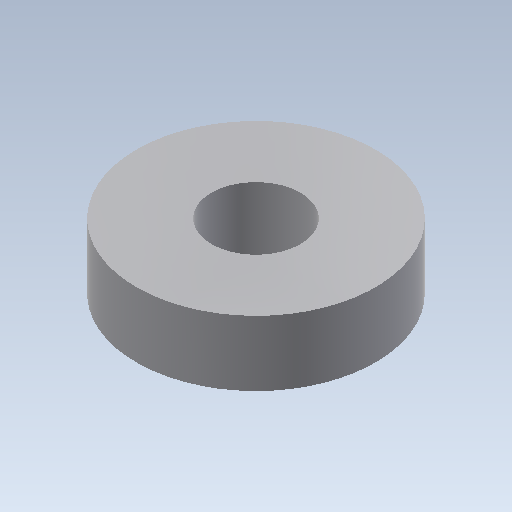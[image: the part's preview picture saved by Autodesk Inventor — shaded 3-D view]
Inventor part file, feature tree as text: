
AUTODESK INVENTOR PART (.ipt)
format: ipt  version: 2020 (Build 240168000, 168)  size: 86,016 bytes
history: native  units: mm
features: extrude x1, sketch x1
ambient origin geometry x8: Origin, YZ Plane, XZ Plane, XY Plane, X Axis, Y Axis, Z Axis, Center Point
bodies: Solid1 (feature_tree)
feature tree (2):
  extrude  "Extrusion1"  Depth=3.0mm
  sketch  "Sketch1"  dims[d0=11.0mm d1=4.1mm d2=3.0mm d3=0.0mm]
